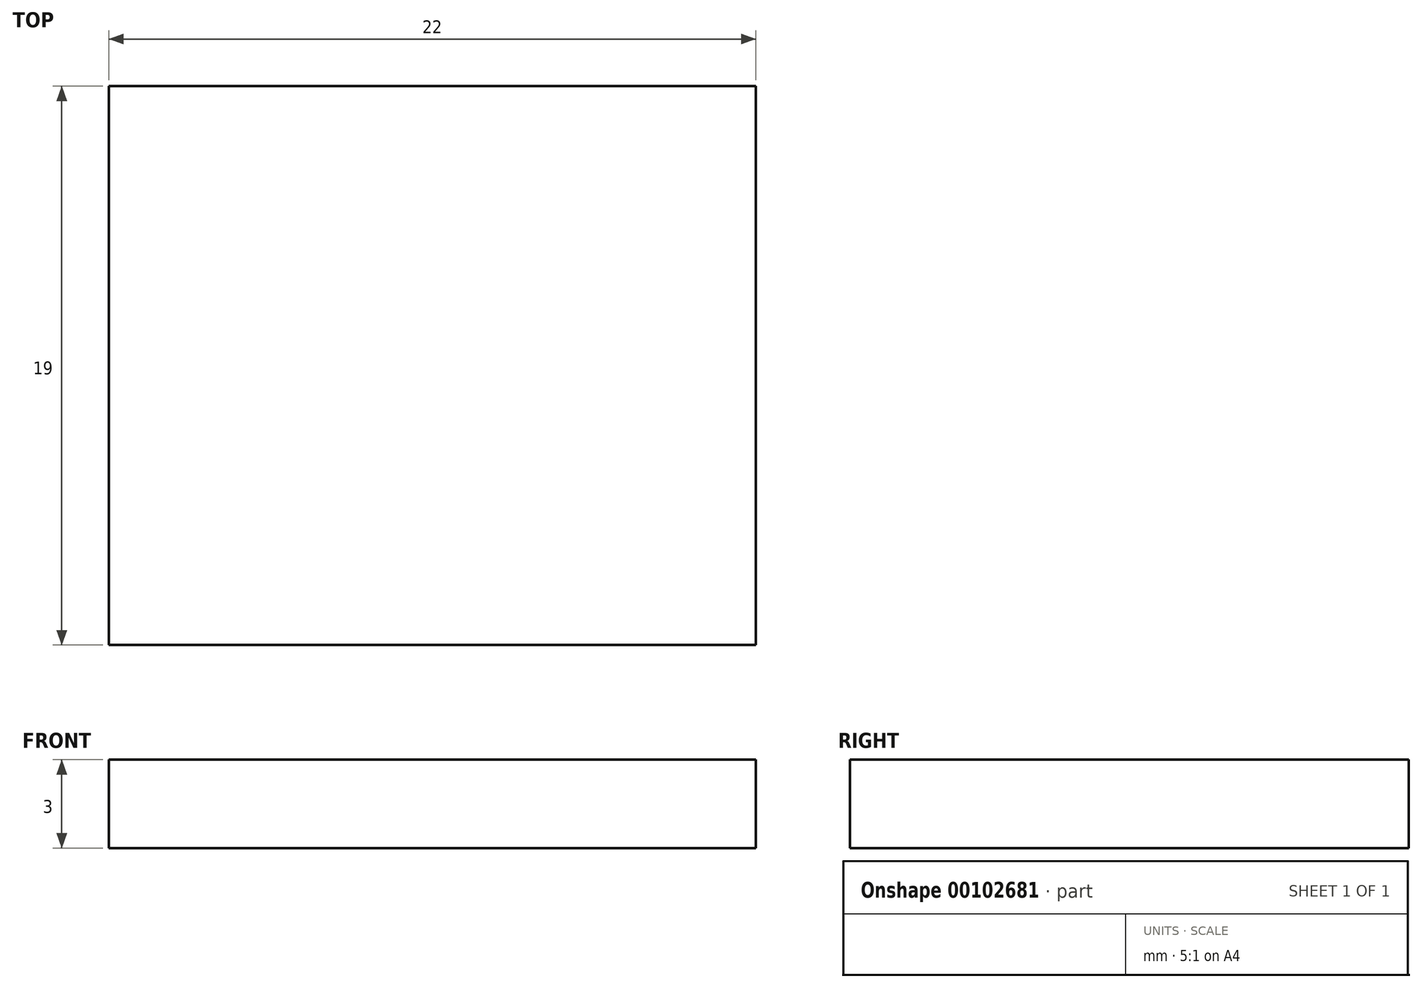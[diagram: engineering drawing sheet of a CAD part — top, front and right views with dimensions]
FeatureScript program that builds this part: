
annotation { "Feature Type Name" : "Feature", "Feature Type Description" : "" }
export const myFeature = defineFeature(function(context is Context, id is Id, definition is map)
    precondition{}
    {
        {
            var Q0;
            Q0=qCreatedBy(makeId("Top.planeOp"),FACE);
            var sketch = newSketch(context, id + "F0", { "sketchPlane" : qUnion([Q0])});
            skLineSegment(sketch, "E0.bottom", {"start": v(11, 9.5) * mm, "end": v(-11, 9.5) * mm});
            skLineSegment(sketch, "E0.top", {"start": v(11, -9.5) * mm, "end": v(-11, -9.5) * mm});
            skLineSegment(sketch, "E0.left", {"start": v(11, 9.5) * mm, "end": v(11, -9.5) * mm});
            skLineSegment(sketch, "E0.right", {"start": v(-11, 9.5) * mm, "end": v(-11, -9.5) * mm});
            skPoint(sketch, "E0.middle", {"position": v(0, 0) * mm});
            skSolve(sketch);
        }
        {
            var Q0;
            Q0=makeQuery(id+"F0.imprint","IMPRINT",FACE,{"disambiguationData":[TD([[makeQuery(id+"F0.imprint","IMPRINT",EDGE,{"derivedFrom":sQuery(id+"F0.wireOp",EDGE,"E0.bottom")}),1.0]])]});
            extrude(context, id + "F1", {"entities" : qUnion([Q0]), "depth" : 3 * mm});
        }
    });
